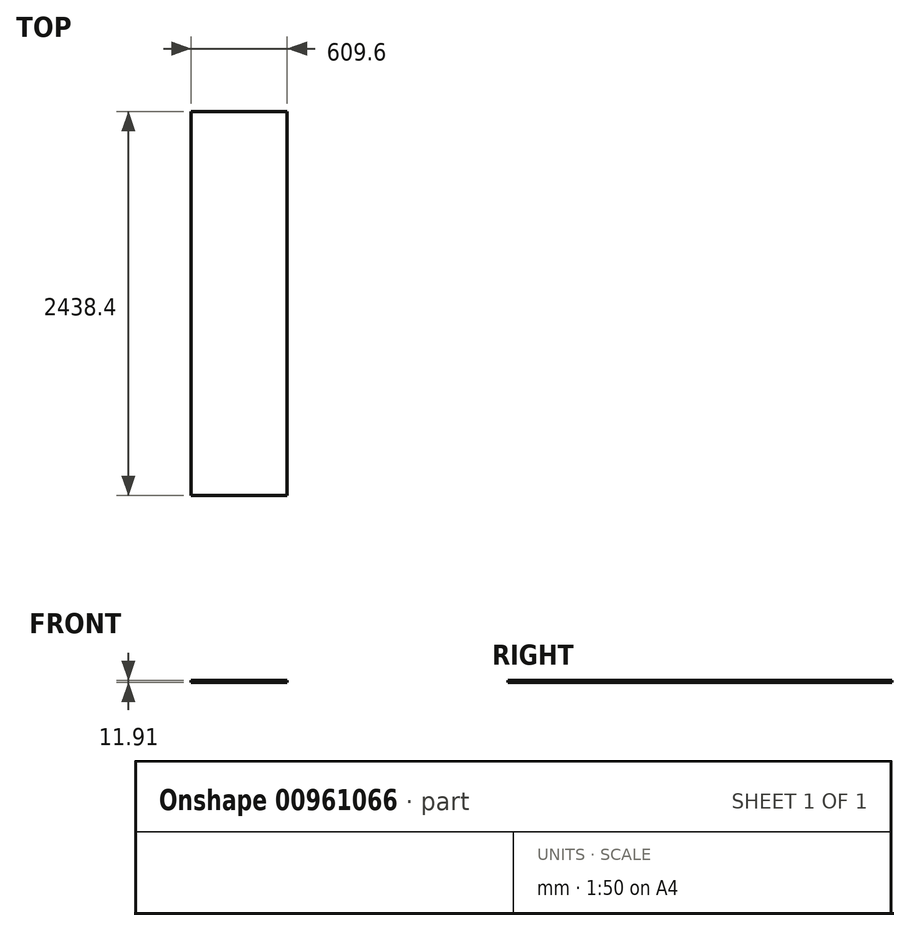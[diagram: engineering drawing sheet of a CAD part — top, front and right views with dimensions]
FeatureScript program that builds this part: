
annotation { "Feature Type Name" : "Feature", "Feature Type Description" : "" }
export const myFeature = defineFeature(function(context is Context, id is Id, definition is map)
    precondition{}
    {
        {
            var Q0;
            Q0=qCreatedBy(makeId("Front.planeOp"),FACE);
            var sketch = newSketch(context, id + "F0", { "sketchPlane" : qUnion([Q0])});
            skLineSegment(sketch, "E0.bottom", {"start": v(-366.63, 36.44) * mm, "end": v(242.97, 36.44) * mm});
            skLineSegment(sketch, "E0.top", {"start": v(-366.63, 48.35) * mm, "end": v(242.97, 48.35) * mm});
            skLineSegment(sketch, "E0.left", {"start": v(-366.63, 36.44) * mm, "end": v(-366.63, 48.35) * mm});
            skLineSegment(sketch, "E0.right", {"start": v(242.97, 36.44) * mm, "end": v(242.97, 48.35) * mm});
            skLineSegment(sketch, "E1.bottom", {"start": v(-1762, 47.6) * mm, "end": v(-542.8, 47.6) * mm});
            skLineSegment(sketch, "E1.top", {"start": v(-1762, 59.5) * mm, "end": v(-542.8, 59.5) * mm});
            skLineSegment(sketch, "E1.left", {"start": v(-1762, 47.6) * mm, "end": v(-1762, 59.5) * mm});
            skLineSegment(sketch, "E1.right", {"start": v(-542.8, 47.6) * mm, "end": v(-542.8, 59.5) * mm});
            skSolve(sketch);
        }
        {
            var Q0;
            Q0=makeQuery(id+"F0.imprint","IMPRINT",FACE,{"disambiguationData":[TD([[makeQuery(id+"F0.imprint","IMPRINT",EDGE,{"derivedFrom":sQuery(id+"F0.wireOp",EDGE,"E0.bottom")}),1.0]])]});
            extrude(context, id + "F1", {"entities" : qUnion([Q0]), "depth" : 2438.4 * mm, "offsetDistance" : 25.4 * mm});
        }
    });
